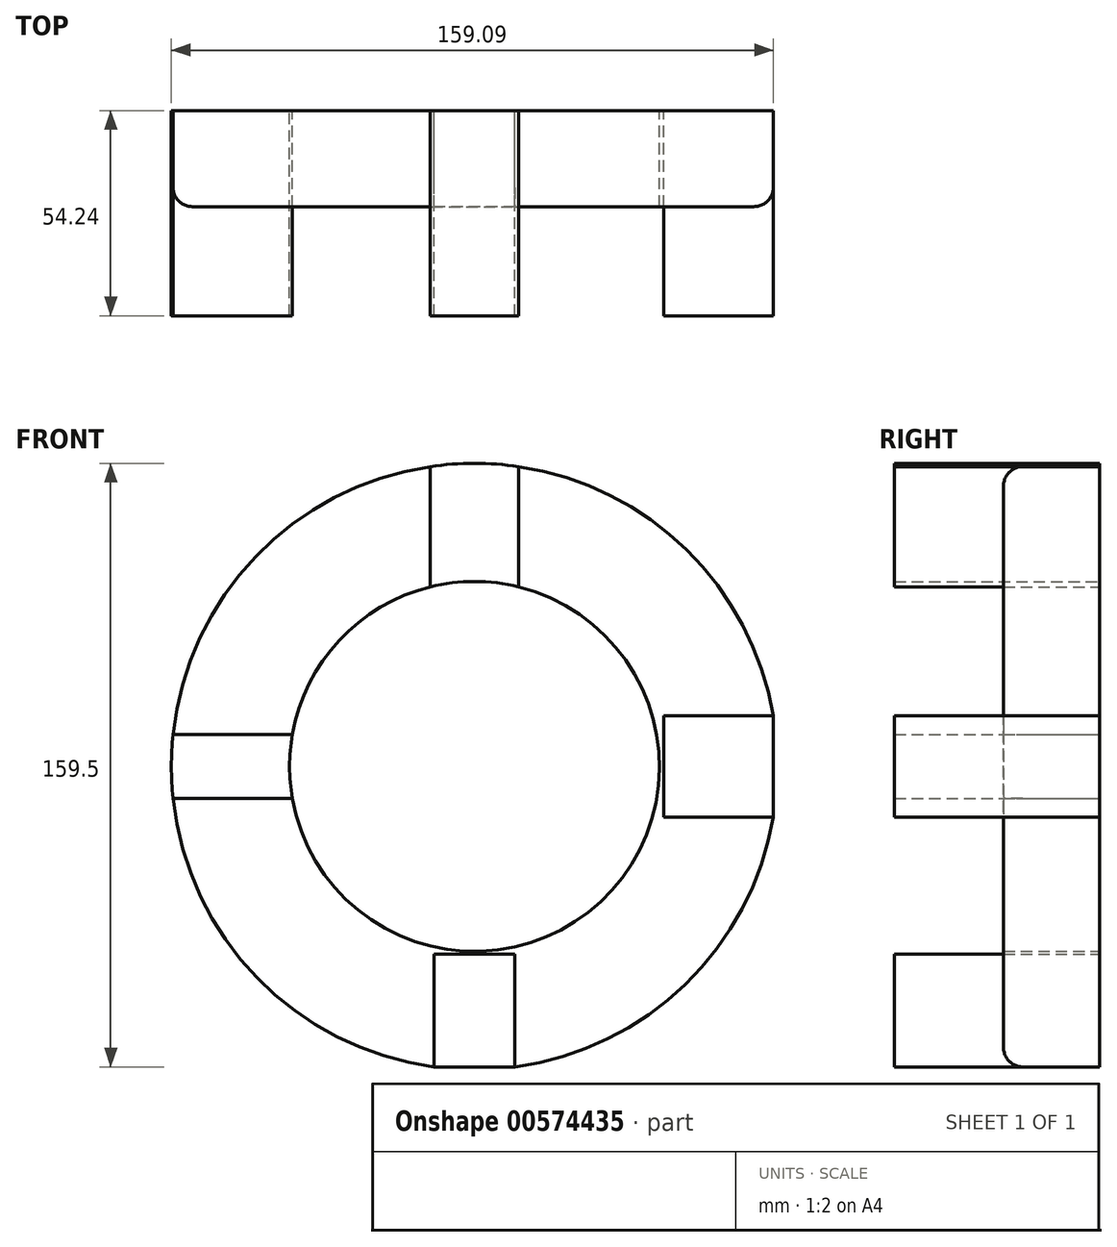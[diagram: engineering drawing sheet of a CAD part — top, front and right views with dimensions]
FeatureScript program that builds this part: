
annotation { "Feature Type Name" : "Feature", "Feature Type Description" : "" }
export const myFeature = defineFeature(function(context is Context, id is Id, definition is map)
    precondition{}
    {
        {
            var Q0;
            Q0=qCreatedBy(makeId("Front.planeOp"),FACE);
            var sketch = newSketch(context, id + "F0", { "sketchPlane" : qUnion([Q0])});
            skCircle(sketch, "E0", {"center": v(0, 0) * mm, "radius": 48.87 * mm});
            skCircle(sketch, "E1", {"center": v(0, 0) * mm, "radius": 80.1 * mm});
            skLineSegment(sketch, "E2", {"start": v(48.87, 0) * mm, "end": v(80.1, 0) * mm});
            skLineSegment(sketch, "E3", {"start": v(0, 48.87) * mm, "end": v(0, 80.1) * mm});
            skLineSegment(sketch, "E4", {"start": v(-48.87, 0) * mm, "end": v(-80.1, 0) * mm});
            skLineSegment(sketch, "E5", {"start": v(0, -48.87) * mm, "end": v(0, -80.1) * mm});
            skLineSegment(sketch, "E6.bottom", {"start": v(-48.14, -8.42) * mm, "end": v(-80.84, -8.42) * mm});
            skLineSegment(sketch, "E6.top", {"start": v(-48.14, 8.42) * mm, "end": v(-80.84, 8.42) * mm});
            skLineSegment(sketch, "E6.left", {"start": v(-48.14, -8.42) * mm, "end": v(-48.14, 8.42) * mm});
            skLineSegment(sketch, "E6.right", {"start": v(-80.84, -8.42) * mm, "end": v(-80.84, 8.42) * mm});
            skPoint(sketch, "E6.middle", {"position": v(-64.49, 0) * mm});
            skLineSegment(sketch, "E7.bottom", {"start": v(10.7, -79.39) * mm, "end": v(-10.7, -79.39) * mm});
            skLineSegment(sketch, "E7.top", {"start": v(10.7, -49.59) * mm, "end": v(-10.7, -49.59) * mm});
            skLineSegment(sketch, "E7.left", {"start": v(10.7, -79.39) * mm, "end": v(10.7, -49.59) * mm});
            skLineSegment(sketch, "E7.right", {"start": v(-10.7, -79.39) * mm, "end": v(-10.7, -49.59) * mm});
            skPoint(sketch, "E7.middle", {"position": v(0, -64.49) * mm});
            skLineSegment(sketch, "E8.bottom", {"start": v(78.98, 13.36) * mm, "end": v(50, 13.36) * mm});
            skLineSegment(sketch, "E8.top", {"start": v(78.98, -13.36) * mm, "end": v(50, -13.36) * mm});
            skLineSegment(sketch, "E8.left", {"start": v(78.98, 13.36) * mm, "end": v(78.98, -13.36) * mm});
            skLineSegment(sketch, "E8.right", {"start": v(50, 13.36) * mm, "end": v(50, -13.36) * mm});
            skPoint(sketch, "E8.middle", {"position": v(64.49, 0) * mm});
            skLineSegment(sketch, "E9.bottom", {"start": v(11.72, 47.44) * mm, "end": v(-11.72, 47.44) * mm});
            skLineSegment(sketch, "E9.top", {"start": v(11.72, 81.53) * mm, "end": v(-11.72, 81.53) * mm});
            skLineSegment(sketch, "E9.left", {"start": v(11.72, 47.44) * mm, "end": v(11.72, 81.53) * mm});
            skLineSegment(sketch, "E9.right", {"start": v(-11.72, 47.44) * mm, "end": v(-11.72, 81.53) * mm});
            skPoint(sketch, "E9.middle", {"position": v(0, 64.49) * mm});
            skSolve(sketch);
        }
        {
            var Q0;
            {var subQ0=sQuery(id+"F0.wireOp",EDGE,"E8.bottom");Q0=makeQuery(id+"F0.imprint","IMPRINT",FACE,{"disambiguationData":[TD([[makeQuery(id+"F0.imprint","IMPRINT",EDGE,{"derivedFrom":subQ0}),-1.0]])]});}
            var Q1;
            {var subQ3=sQuery(id+"F0.wireOp",EDGE,"E9.right");var subQ5=sQuery(id+"F0.wireOp",EDGE,"E1");var subQ6=makeQuery(id+"F0.imprint","INTERSECT",VERTEX,{"derivedFrom":[subQ5,subQ3]});Q1=makeQuery(id+"F0.imprint","IMPRINT",FACE,{"disambiguationData":[TD([[makeQuery(id+"F0.imprint","IMPRINT",EDGE,{"disambiguationData":[TD([[subQ6,-1.0]])],"derivedFrom":subQ5}),1.0]])]});}
            var Q2;
            {var subQ5=sQuery(id+"F0.wireOp",EDGE,"E7.left");Q2=makeQuery(id+"F0.imprint","IMPRINT",FACE,{"disambiguationData":[TD([[makeQuery(id+"F0.imprint","IMPRINT",EDGE,{"derivedFrom":subQ5}),-1.0]])]});}
            var Q3;
            {var subQ7=sQuery(id+"F0.wireOp",EDGE,"E7.right");Q3=makeQuery(id+"F0.imprint","IMPRINT",FACE,{"disambiguationData":[TD([[makeQuery(id+"F0.imprint","IMPRINT",EDGE,{"derivedFrom":subQ7}),1.0]])]});}
            extrude(context, id + "F1", {"entities" : qUnion([Q0, Q1, Q2, Q3]), "depth" : 25.4 * mm, "offsetDistance" : 25.4 * mm});
        }
        {
            var Q0;
            {var subQ0=sQuery(id+"F0.wireOp",EDGE,"E3");Q0=makeQuery(id+"F0.imprint","IMPRINT",FACE,{"disambiguationData":[TD([[makeQuery(id+"F0.imprint","IMPRINT",EDGE,{"derivedFrom":subQ0}),-1.0]])]});}
            var Q1;
            {var subQ0=sQuery(id+"F0.wireOp",EDGE,"E3");Q1=makeQuery(id+"F0.imprint","IMPRINT",FACE,{"disambiguationData":[TD([[makeQuery(id+"F0.imprint","IMPRINT",EDGE,{"derivedFrom":subQ0}),1.0]])]});}
            var Q2;
            {var subQ5=sQuery(id+"F0.wireOp",EDGE,"E8.top");Q2=makeQuery(id+"F0.imprint","IMPRINT",FACE,{"disambiguationData":[TD([[makeQuery(id+"F0.imprint","IMPRINT",EDGE,{"derivedFrom":subQ5}),-1.0]])]});}
            var Q3;
            {var subQ5=sQuery(id+"F0.wireOp",EDGE,"E8.bottom");Q3=makeQuery(id+"F0.imprint","IMPRINT",FACE,{"disambiguationData":[TD([[makeQuery(id+"F0.imprint","IMPRINT",EDGE,{"derivedFrom":subQ5}),1.0]])]});}
            var Q4;
            {var subQ0=sQuery(id+"F0.wireOp",EDGE,"E4");Q4=makeQuery(id+"F0.imprint","IMPRINT",FACE,{"disambiguationData":[TD([[makeQuery(id+"F0.imprint","IMPRINT",EDGE,{"derivedFrom":subQ0}),1.0]])]});}
            var Q5;
            {var subQ0=sQuery(id+"F0.wireOp",EDGE,"E4");Q5=makeQuery(id+"F0.imprint","IMPRINT",FACE,{"disambiguationData":[TD([[makeQuery(id+"F0.imprint","IMPRINT",EDGE,{"derivedFrom":subQ0}),-1.0]])]});}
            var Q6;
            {var subQ5=sQuery(id+"F0.wireOp",EDGE,"E7.left");Q6=makeQuery(id+"F0.imprint","IMPRINT",FACE,{"disambiguationData":[TD([[makeQuery(id+"F0.imprint","IMPRINT",EDGE,{"derivedFrom":subQ5}),1.0]])]});}
            var Q7;
            {var subQ5=sQuery(id+"F0.wireOp",EDGE,"E7.right");Q7=makeQuery(id+"F0.imprint","IMPRINT",FACE,{"disambiguationData":[TD([[makeQuery(id+"F0.imprint","IMPRINT",EDGE,{"derivedFrom":subQ5}),-1.0]])]});}
            extrude(context, id + "F2", {"entities" : qUnion([Q0, Q1, Q2, Q3, Q4, Q5, Q6, Q7]), "depth" : 54.24 * mm, "offsetDistance" : 25.4 * mm});
        }
        {
            var Q0;
            {var subQ0=sQuery(id+"F0.wireOp",EDGE,"E1");Q0=makeQuery(id+"F1.opExtrude","CAP_EDGE",EDGE,{"disambiguationData":[OSD([subQ0]),TDD([makeQuery(id+"F0.imprint","IMPRINT",EDGE,{"disambiguationData":[TD([[makeQuery(id+"F0.imprint","INTERSECT",VERTEX,{"derivedFrom":[subQ0,sQuery(id+"F0.wireOp",EDGE,"E6.bottom")]}),-1.0]])],"derivedFrom":subQ0})])],"isStart":false});}
            var Q1;
            {var subQ0=sQuery(id+"F0.wireOp",EDGE,"E1");Q1=makeQuery(id+"F1.opExtrude","CAP_EDGE",EDGE,{"disambiguationData":[OSD([subQ0]),TDD([makeQuery(id+"F0.imprint","IMPRINT",EDGE,{"disambiguationData":[TD([[makeQuery(id+"F0.imprint","INTERSECT",VERTEX,{"derivedFrom":[subQ0,sQuery(id+"F0.wireOp",EDGE,"E9.right")]}),-1.0]])],"derivedFrom":subQ0})])],"isStart":false});}
            var Q2;
            {var subQ0=sQuery(id+"F0.wireOp",EDGE,"E1");Q2=makeQuery(id+"F1.opExtrude","CAP_EDGE",EDGE,{"disambiguationData":[OSD([subQ0]),TDD([makeQuery(id+"F0.imprint","IMPRINT",EDGE,{"disambiguationData":[TD([[makeQuery(id+"F0.imprint","INTERSECT",VERTEX,{"derivedFrom":[subQ0,sQuery(id+"F0.wireOp",EDGE,"E9.left")]}),1.0]])],"derivedFrom":subQ0})])],"isStart":false});}
            var Q3;
            {var subQ0=sQuery(id+"F0.wireOp",EDGE,"E1");Q3=makeQuery(id+"F1.opExtrude","CAP_EDGE",EDGE,{"disambiguationData":[OSD([subQ0]),TDD([makeQuery(id+"F0.imprint","IMPRINT",EDGE,{"disambiguationData":[TD([[makeQuery(id+"F0.imprint","INTERSECT",VERTEX,{"derivedFrom":[subQ0,sQuery(id+"F0.wireOp",EDGE,"E7.bottom"),sQuery(id+"F0.wireOp",EDGE,"E7.left")]}),-1.0]])],"derivedFrom":subQ0})])],"isStart":false});}
            fillet(context, id + "F3", {"entities" : qUnion([Q0, Q1, Q2, Q3]), "radius" : 5.08 * mm, "tangentPropagation" : true, "allowEdgeOverflow" : false});
        }
    });
